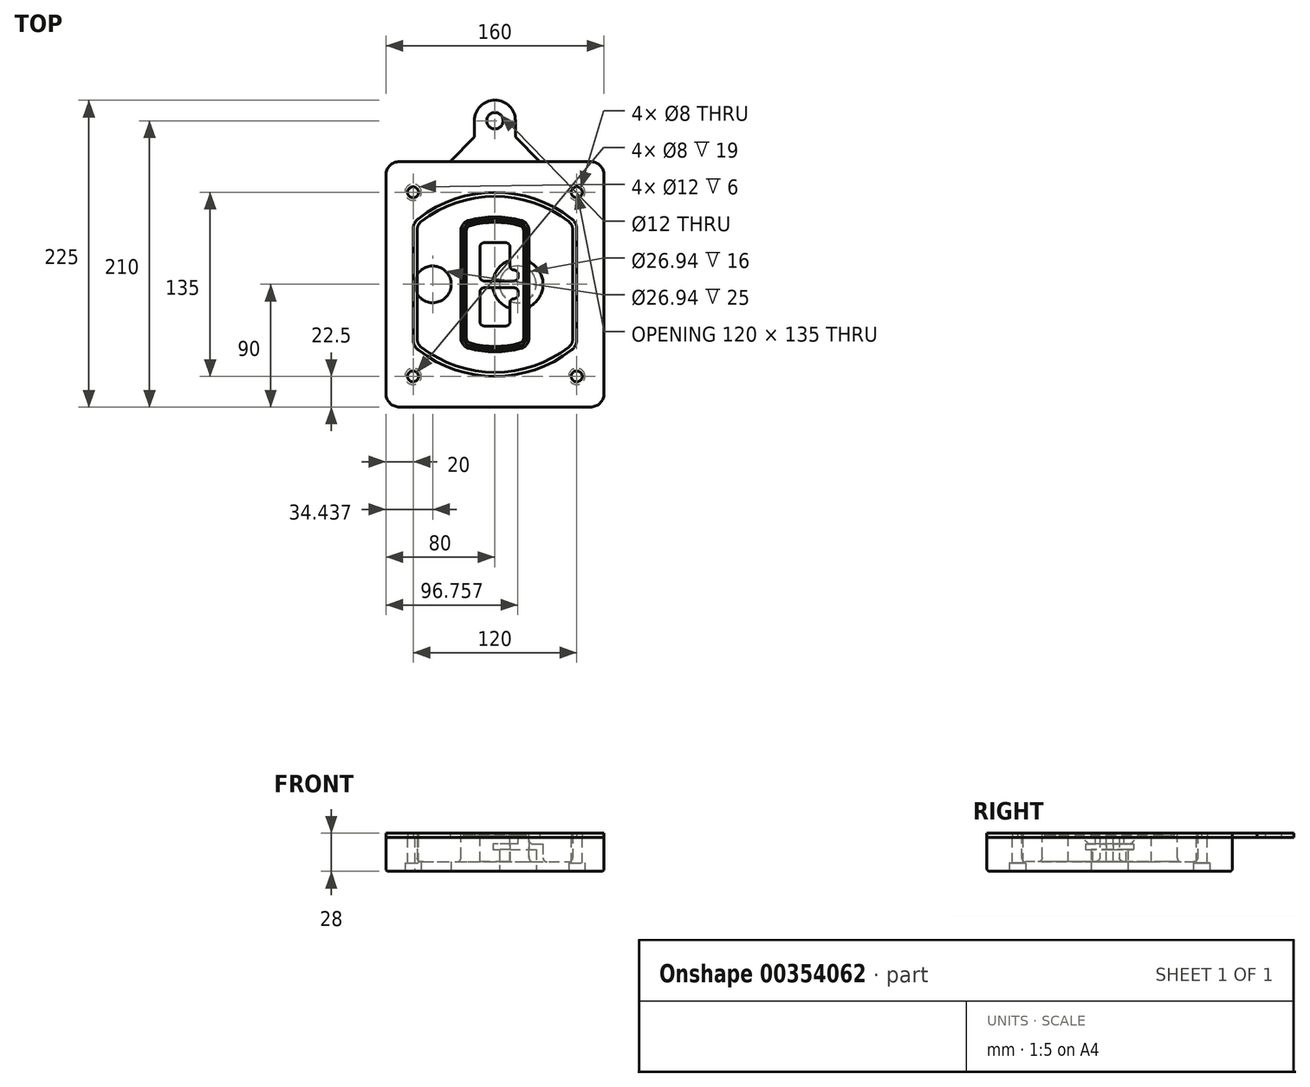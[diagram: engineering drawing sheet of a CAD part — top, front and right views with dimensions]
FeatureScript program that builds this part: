
annotation { "Feature Type Name" : "Feature", "Feature Type Description" : "" }
export const myFeature = defineFeature(function(context is Context, id is Id, definition is map)
    precondition{}
    {
        {
            var Q0;
            Q0=qCreatedBy(makeId("Top.planeOp"),FACE);
            var sketch = newSketch(context, id + "F0", { "sketchPlane" : qUnion([Q0])});
            skPoint(sketch, "E0.rect.middle", {"position": v(0, 0) * mm});
            skLineSegment(sketch, "E1.bottom", {"start": v(-70, -90) * mm, "end": v(70, -90) * mm});
            skLineSegment(sketch, "E1.top", {"start": v(-70, 90) * mm, "end": v(70, 90) * mm});
            skLineSegment(sketch, "E1.left", {"start": v(-80, -80) * mm, "end": v(-80, 80) * mm});
            skLineSegment(sketch, "E1.right", {"start": v(80, -80) * mm, "end": v(80, 80) * mm});
            skLineSegment(sketch, "E2", {"start": v(-80, 90) * mm, "end": v(80, -90) * mm, "construction": true});
            skLineSegment(sketch, "E3", {"start": v(80, 90) * mm, "end": v(-80, -90) * mm, "construction": true});
            skCircle(sketch, "E4", {"center": v(-60, 67.5) * mm, "radius": 4 * mm});
            skCircle(sketch, "E5", {"center": v(60, 67.5) * mm, "radius": 4 * mm});
            skCircle(sketch, "E6", {"center": v(60, -67.5) * mm, "radius": 4 * mm});
            skCircle(sketch, "E7", {"center": v(-60, -67.5) * mm, "radius": 4 * mm});
            skLineSegment(sketch, "E8", {"start": v(-60, 67.5) * mm, "end": v(60, 67.5) * mm, "construction": true});
            skLineSegment(sketch, "E9", {"start": v(60, 67.5) * mm, "end": v(60, -67.5) * mm, "construction": true});
            skLineSegment(sketch, "E10", {"start": v(60, -67.5) * mm, "end": v(-60, -67.5) * mm, "construction": true});
            skLineSegment(sketch, "E11", {"start": v(-60, -67.5) * mm, "end": v(-60, 67.5) * mm, "construction": true});
            skLineSegment(sketch, "E12", {"start": v(-60, 40.3) * mm, "end": v(-60, -40.3) * mm});
            skLineSegment(sketch, "E13", {"start": v(60, 40.3) * mm, "end": v(60, -40.3) * mm});
            skArc(sketch, "E14", {"start": v(56.15, 48.18) * mm, "mid": v(0, 67.5) * mm, "end": v(-56.15, 48.18) * mm});
            skArc(sketch, "E15", {"start": v(-56.15, -48.18) * mm, "mid": v(0, -67.5) * mm, "end": v(56.15, -48.18) * mm});
            skLineSegment(sketch, "E16", {"start": v(-60, 0) * mm, "end": v(60, 0) * mm, "construction": true});
            skPoint(sketch, "E17.visualSharp", {"position": v(-60, -45) * mm});
            skArc(sketch, "E17.filletArc", {"start": v(-60, -40.3) * mm, "mid": v(-58.99, -44.68) * mm, "end": v(-56.15, -48.18) * mm});
            skPoint(sketch, "E18.visualSharp", {"position": v(-60, 45) * mm});
            skArc(sketch, "E18.filletArc", {"start": v(-56.15, 48.18) * mm, "mid": v(-58.99, 44.68) * mm, "end": v(-60, 40.3) * mm});
            skPoint(sketch, "E19.visualSharp", {"position": v(60, 45) * mm});
            skArc(sketch, "E19.filletArc", {"start": v(60, 40.3) * mm, "mid": v(58.99, 44.68) * mm, "end": v(56.15, 48.18) * mm});
            skPoint(sketch, "E20.visualSharp", {"position": v(60, -45) * mm});
            skArc(sketch, "E20.filletArc", {"start": v(56.15, -48.18) * mm, "mid": v(58.99, -44.68) * mm, "end": v(60, -40.3) * mm});
            skPoint(sketch, "E21.visualSharp", {"position": v(-80, 90) * mm});
            skArc(sketch, "E21.filletArc", {"start": v(-70, 90) * mm, "mid": v(-77.07, 87.07) * mm, "end": v(-80, 80) * mm});
            skPoint(sketch, "E22.visualSharp", {"position": v(80, 90) * mm});
            skArc(sketch, "E22.filletArc", {"start": v(80, 80) * mm, "mid": v(77.07, 87.07) * mm, "end": v(70, 90) * mm});
            skPoint(sketch, "E23.visualSharp", {"position": v(80, -90) * mm});
            skArc(sketch, "E23.filletArc", {"start": v(70, -90) * mm, "mid": v(77.07, -87.07) * mm, "end": v(80, -80) * mm});
            skPoint(sketch, "E24.visualSharp", {"position": v(-80, -90) * mm});
            skArc(sketch, "E24.filletArc", {"start": v(-80, -80) * mm, "mid": v(-77.07, -87.07) * mm, "end": v(-70, -90) * mm});
            skArc(sketch, "E25.0", {"start": v(57, 40.3) * mm, "mid": v(56.3, 43.36) * mm, "end": v(54.3, 45.81) * mm});
            skLineSegment(sketch, "E25.1", {"start": v(57, 40.3) * mm, "end": v(57, -40.3) * mm});
            skArc(sketch, "E25.2", {"start": v(54.3, -45.81) * mm, "mid": v(56.3, -43.36) * mm, "end": v(57, -40.3) * mm});
            skArc(sketch, "E25.3", {"start": v(-54.3, -45.81) * mm, "mid": v(0, -64.5) * mm, "end": v(54.3, -45.81) * mm});
            skArc(sketch, "E25.4", {"start": v(-57, -40.3) * mm, "mid": v(-56.3, -43.36) * mm, "end": v(-54.3, -45.81) * mm});
            skArc(sketch, "E25.5", {"start": v(54.3, 45.81) * mm, "mid": v(0, 64.5) * mm, "end": v(-54.3, 45.81) * mm});
            skLineSegment(sketch, "E25.6", {"start": v(-57, 40.3) * mm, "end": v(-57, -40.3) * mm});
            skArc(sketch, "E25.7", {"start": v(-54.3, 45.81) * mm, "mid": v(-56.3, 43.36) * mm, "end": v(-57, 40.3) * mm});
            skArc(sketch, "E26.0", {"start": v(-58.62, 51.33) * mm, "mid": v(-62.58, 46.43) * mm, "end": v(-64, 40.3) * mm});
            skArc(sketch, "E26.1", {"start": v(58.62, 51.33) * mm, "mid": v(0, 71.5) * mm, "end": v(-58.62, 51.33) * mm});
            skArc(sketch, "E26.2", {"start": v(64, 40.3) * mm, "mid": v(62.58, 46.43) * mm, "end": v(58.62, 51.33) * mm});
            skLineSegment(sketch, "E26.3", {"start": v(64, 40.3) * mm, "end": v(64, -40.3) * mm});
            skArc(sketch, "E26.4", {"start": v(58.62, -51.33) * mm, "mid": v(62.58, -46.43) * mm, "end": v(64, -40.3) * mm});
            skLineSegment(sketch, "E26.5", {"start": v(-64, 40.3) * mm, "end": v(-64, -40.3) * mm});
            skArc(sketch, "E26.6", {"start": v(-58.62, -51.33) * mm, "mid": v(0, -71.5) * mm, "end": v(58.62, -51.33) * mm});
            skArc(sketch, "E26.7", {"start": v(-64, -40.3) * mm, "mid": v(-62.58, -46.43) * mm, "end": v(-58.62, -51.33) * mm});
            skSolve(sketch);
        }
        {
            var Q0;
            Q0=makeQuery(id+"F0.imprint","IMPRINT",FACE,{"disambiguationData":[TD([[makeQuery(id+"F0.imprint","IMPRINT",EDGE,{"derivedFrom":sQuery(id+"F0.wireOp",EDGE,"E1.bottom")}),1.0]])]});
            var Q1;
            Q1=makeQuery(id+"F0.imprint","IMPRINT",FACE,{"disambiguationData":[TD([[makeQuery(id+"F0.imprint","IMPRINT",EDGE,{"derivedFrom":sQuery(id+"F0.wireOp",EDGE,"E12")}),1.0]])]});
            var Q2;
            Q2=makeQuery(id+"F0.imprint","IMPRINT",FACE,{"disambiguationData":[TD([[makeQuery(id+"F0.imprint","IMPRINT",EDGE,{"derivedFrom":sQuery(id+"F0.wireOp",EDGE,"E25.0")}),1.0]])]});
            var Q3;
            Q3=makeQuery(id+"F0.imprint","IMPRINT",FACE,{"disambiguationData":[TD([[makeQuery(id+"F0.imprint","IMPRINT",EDGE,{"derivedFrom":sQuery(id+"F0.wireOp",EDGE,"E12")}),-1.0]])]});
            extrude(context, id + "F1", {"entities" : qUnion([Q0, Q1, Q2, Q3]), "oppositeDirection" : true, "depth" : 25 * mm});
        }
        {
            var Q0;
            Q0=makeQuery(id+"F0.imprint","IMPRINT",FACE,{"disambiguationData":[TD([[makeQuery(id+"F0.imprint","IMPRINT",EDGE,{"derivedFrom":sQuery(id+"F0.wireOp",EDGE,"E12")}),1.0]])]});
            extrude(context, id + "F2", {"entities" : qUnion([Q0]), "operationType" : NewBodyOperationType.ADD, "depth" : 3 * mm});
        }
        {
            var Q0;
            Q0=makeQuery(id+"F0.imprint","IMPRINT",FACE,{"disambiguationData":[TD([[makeQuery(id+"F0.imprint","IMPRINT",EDGE,{"derivedFrom":sQuery(id+"F0.wireOp",EDGE,"E25.0")}),1.0]])]});
            extrude(context, id + "F3", {"entities" : qUnion([Q0]), "operationType" : NewBodyOperationType.REMOVE, "oppositeDirection" : true, "depth" : 18 * mm});
        }
        {
            var Q0;
            Q0=makeQuery(id+"F2.opExtrude","CAP_FACE",FACE,{"disambiguationData":[OSD([sQuery(id+"F0.wireOp",EDGE,"E12"),sQuery(id+"F0.wireOp",EDGE,"E13"),sQuery(id+"F0.wireOp",EDGE,"E14"),sQuery(id+"F0.wireOp",EDGE,"E15"),sQuery(id+"F0.wireOp",EDGE,"E17.filletArc"),sQuery(id+"F0.wireOp",EDGE,"E18.filletArc"),sQuery(id+"F0.wireOp",EDGE,"E19.filletArc"),sQuery(id+"F0.wireOp",EDGE,"E20.filletArc"),sQuery(id+"F0.wireOp",EDGE,"E25.0"),sQuery(id+"F0.wireOp",EDGE,"E25.1"),sQuery(id+"F0.wireOp",EDGE,"E25.2"),sQuery(id+"F0.wireOp",EDGE,"E25.3"),sQuery(id+"F0.wireOp",EDGE,"E25.4"),sQuery(id+"F0.wireOp",EDGE,"E25.5"),sQuery(id+"F0.wireOp",EDGE,"E25.6"),sQuery(id+"F0.wireOp",EDGE,"E25.7")])],"isStart":false});
            var sketch = newSketch(context, id + "F4", { "sketchPlane" : qUnion([Q0])});
            skArc(sketch, "E27.0", {"start": v(-19.08, -46.97) * mm, "mid": v(0, -49.5) * mm, "end": v(19.08, -46.97) * mm});
            skArc(sketch, "E28.0", {"start": v(19.08, 46.97) * mm, "mid": v(0, 49.5) * mm, "end": v(-19.08, 46.97) * mm});
            skLineSegment(sketch, "E29", {"start": v(-25, 39.25) * mm, "end": v(-25, -39.25) * mm});
            skLineSegment(sketch, "E30", {"start": v(25, 39.25) * mm, "end": v(25, -39.25) * mm});
            skLineSegment(sketch, "E31", {"start": v(-25, 45.1) * mm, "end": v(25, 45.1) * mm, "construction": true});
            skLineSegment(sketch, "E32", {"start": v(-25, -45.1) * mm, "end": v(25, -45.1) * mm, "construction": true});
            skPoint(sketch, "E33.visualSharp", {"position": v(-25, 45.1) * mm});
            skArc(sketch, "E33.filletArc", {"start": v(-19.08, 46.97) * mm, "mid": v(-23.35, 44.11) * mm, "end": v(-25, 39.25) * mm});
            skPoint(sketch, "E34.visualSharp", {"position": v(25, 45.1) * mm});
            skArc(sketch, "E34.filletArc", {"start": v(25, 39.25) * mm, "mid": v(23.35, 44.11) * mm, "end": v(19.08, 46.97) * mm});
            skPoint(sketch, "E35.visualSharp", {"position": v(25, -45.1) * mm});
            skArc(sketch, "E35.filletArc", {"start": v(19.08, -46.97) * mm, "mid": v(23.35, -44.11) * mm, "end": v(25, -39.25) * mm});
            skPoint(sketch, "E36.visualSharp", {"position": v(-25, -45.1) * mm});
            skArc(sketch, "E36.filletArc", {"start": v(-25, -39.25) * mm, "mid": v(-23.35, -44.11) * mm, "end": v(-19.08, -46.97) * mm});
            skArc(sketch, "E37.0", {"start": v(54.3, 45.81) * mm, "mid": v(0, 64.5) * mm, "end": v(-54.3, 45.81) * mm});
            skArc(sketch, "E37.1", {"start": v(-54.3, 45.81) * mm, "mid": v(-56.3, 43.36) * mm, "end": v(-57, 40.3) * mm});
            skLineSegment(sketch, "E37.2", {"start": v(-57, 40.3) * mm, "end": v(-57, -40.3) * mm});
            skArc(sketch, "E37.3", {"start": v(-57, -40.3) * mm, "mid": v(-56.3, -43.36) * mm, "end": v(-54.3, -45.81) * mm});
            skArc(sketch, "E37.4", {"start": v(-54.3, -45.81) * mm, "mid": v(0, -64.5) * mm, "end": v(54.3, -45.81) * mm});
            skArc(sketch, "E37.5", {"start": v(54.3, -45.81) * mm, "mid": v(56.3, -43.36) * mm, "end": v(57, -40.3) * mm});
            skLineSegment(sketch, "E37.6", {"start": v(57, 40.3) * mm, "end": v(57, -40.3) * mm});
            skArc(sketch, "E37.7", {"start": v(57, 40.3) * mm, "mid": v(56.3, 43.36) * mm, "end": v(54.3, 45.81) * mm});
            skLineSegment(sketch, "E38.0", {"start": v(23, 39.25) * mm, "end": v(23, -39.25) * mm});
            skArc(sketch, "E38.1", {"start": v(18.56, -45.04) * mm, "mid": v(21.76, -42.9) * mm, "end": v(23, -39.25) * mm});
            skArc(sketch, "E38.2", {"start": v(-18.56, -45.04) * mm, "mid": v(0, -47.5) * mm, "end": v(18.56, -45.04) * mm});
            skArc(sketch, "E38.3", {"start": v(-23, -39.25) * mm, "mid": v(-21.76, -42.9) * mm, "end": v(-18.56, -45.04) * mm});
            skLineSegment(sketch, "E38.4", {"start": v(-23, 39.25) * mm, "end": v(-23, -39.25) * mm});
            skArc(sketch, "E38.5", {"start": v(23, 39.25) * mm, "mid": v(21.76, 42.9) * mm, "end": v(18.56, 45.04) * mm});
            skArc(sketch, "E38.6", {"start": v(-18.56, 45.04) * mm, "mid": v(-21.76, 42.9) * mm, "end": v(-23, 39.25) * mm});
            skArc(sketch, "E38.7", {"start": v(18.56, 45.04) * mm, "mid": v(0, 47.5) * mm, "end": v(-18.56, 45.04) * mm});
            skArc(sketch, "E39.0", {"start": v(21, 39.25) * mm, "mid": v(20.18, 41.68) * mm, "end": v(18.04, 43.1) * mm});
            skLineSegment(sketch, "E39.1", {"start": v(21, 39.25) * mm, "end": v(21, -39.25) * mm});
            skArc(sketch, "E39.2", {"start": v(18.04, -43.1) * mm, "mid": v(20.18, -41.68) * mm, "end": v(21, -39.25) * mm});
            skArc(sketch, "E39.3", {"start": v(-18.04, -43.1) * mm, "mid": v(0, -45.5) * mm, "end": v(18.04, -43.1) * mm});
            skArc(sketch, "E39.4", {"start": v(-21, -39.25) * mm, "mid": v(-20.18, -41.68) * mm, "end": v(-18.04, -43.1) * mm});
            skArc(sketch, "E39.5", {"start": v(18.04, 43.1) * mm, "mid": v(0, 45.5) * mm, "end": v(-18.04, 43.1) * mm});
            skLineSegment(sketch, "E39.6", {"start": v(-21, 39.25) * mm, "end": v(-21, -39.25) * mm});
            skArc(sketch, "E39.7", {"start": v(-18.04, 43.1) * mm, "mid": v(-20.18, 41.68) * mm, "end": v(-21, 39.25) * mm});
            skLineSegment(sketch, "E40", {"start": v(-25, 0) * mm, "end": v(25, 0) * mm, "construction": true});
            skLineSegment(sketch, "E41", {"start": v(-11, 5.5) * mm, "end": v(-11, 27.5) * mm});
            skLineSegment(sketch, "E42", {"start": v(-8, 30.5) * mm, "end": v(8, 30.5) * mm});
            skLineSegment(sketch, "E43", {"start": v(11, 27.5) * mm, "end": v(11, 13.5) * mm});
            skLineSegment(sketch, "E44", {"start": v(14, 10.5) * mm, "end": v(14, 10.5) * mm});
            skLineSegment(sketch, "E45", {"start": v(17, 7.5) * mm, "end": v(17, 5.5) * mm});
            skLineSegment(sketch, "E46", {"start": v(14, 2.5) * mm, "end": v(-8, 2.5) * mm});
            skPoint(sketch, "E47.visualSharp", {"position": v(-11, 30.5) * mm});
            skArc(sketch, "E47.filletArc", {"start": v(-8, 30.5) * mm, "mid": v(-10.12, 29.62) * mm, "end": v(-11, 27.5) * mm});
            skPoint(sketch, "E48.visualSharp", {"position": v(11, 30.5) * mm});
            skArc(sketch, "E48.filletArc", {"start": v(11, 27.5) * mm, "mid": v(10.12, 29.62) * mm, "end": v(8, 30.5) * mm});
            skPoint(sketch, "E49.visualSharp", {"position": v(11, 10.5) * mm});
            skArc(sketch, "E49.filletArc", {"start": v(11, 13.5) * mm, "mid": v(11.88, 11.38) * mm, "end": v(14, 10.5) * mm});
            skPoint(sketch, "E50.visualSharp", {"position": v(17, 10.5) * mm});
            skArc(sketch, "E50.filletArc", {"start": v(17, 7.5) * mm, "mid": v(16.12, 9.62) * mm, "end": v(14, 10.5) * mm});
            skPoint(sketch, "E51.visualSharp", {"position": v(17, 2.5) * mm});
            skArc(sketch, "E51.filletArc", {"start": v(14, 2.5) * mm, "mid": v(16.12, 3.38) * mm, "end": v(17, 5.5) * mm});
            skPoint(sketch, "E52.visualSharp", {"position": v(-11, 2.5) * mm});
            skArc(sketch, "E52.filletArc", {"start": v(-11, 5.5) * mm, "mid": v(-10.12, 3.38) * mm, "end": v(-8, 2.5) * mm});
            skLineSegment(sketch, "E53.0.MirrorCS", {"start": v(14, -2.5) * mm, "end": v(-8, -2.5) * mm});
            skArc(sketch, "E54.0.MirrorCS", {"start": v(-11, -5.5) * mm, "mid": v(-10.12, -3.38) * mm, "end": v(-8, -2.5) * mm});
            skLineSegment(sketch, "E55.0.MirrorCS", {"start": v(-11, -5.5) * mm, "end": v(-11, -27.5) * mm});
            skArc(sketch, "E56.0.MirrorCS", {"start": v(-8, -30.5) * mm, "mid": v(-10.12, -29.62) * mm, "end": v(-11, -27.5) * mm});
            skLineSegment(sketch, "E57.0.MirrorCS", {"start": v(-8, -30.5) * mm, "end": v(8, -30.5) * mm});
            skArc(sketch, "E58.0.MirrorCS", {"start": v(11, -27.5) * mm, "mid": v(10.12, -29.62) * mm, "end": v(8, -30.5) * mm});
            skLineSegment(sketch, "E59.0.MirrorCS", {"start": v(11, -27.5) * mm, "end": v(11, -13.5) * mm});
            skArc(sketch, "E60.0.MirrorCS", {"start": v(11, -13.5) * mm, "mid": v(11.88, -11.38) * mm, "end": v(14, -10.5) * mm});
            skArc(sketch, "E61.0.MirrorCS", {"start": v(17, -7.5) * mm, "mid": v(16.12, -9.62) * mm, "end": v(14, -10.5) * mm});
            skLineSegment(sketch, "E62.0.MirrorCS", {"start": v(17, -7.5) * mm, "end": v(17, -5.5) * mm});
            skArc(sketch, "E63.0.MirrorCS", {"start": v(14, -2.5) * mm, "mid": v(16.12, -3.38) * mm, "end": v(17, -5.5) * mm});
            skSolve(sketch);
        }
        {
            var Q0;
            Q0=makeQuery(id+"F4.imprint","IMPRINT",FACE,{"disambiguationData":[TD([[makeQuery(id+"F4.imprint","IMPRINT",EDGE,{"derivedFrom":sQuery(id+"F4.wireOp",EDGE,"E27.0")}),1.0]])]});
            var Q1;
            Q1=makeQuery(id+"F4.imprint","IMPRINT",FACE,{"disambiguationData":[TD([[makeQuery(id+"F4.imprint","IMPRINT",EDGE,{"derivedFrom":sQuery(id+"F4.wireOp",EDGE,"E38.0")}),-1.0]])]});
            var Q2;
            Q2=makeQuery(id+"F4.imprint","IMPRINT",FACE,{"disambiguationData":[TD([[makeQuery(id+"F4.imprint","IMPRINT",EDGE,{"derivedFrom":sQuery(id+"F4.wireOp",EDGE,"E39.0")}),1.0]])]});
            extrude(context, id + "F5", {"entities" : qUnion([Q0, Q1, Q2]), "operationType" : NewBodyOperationType.ADD, "endBound" : BoundingType.UP_TO_NEXT, "oppositeDirection" : true, "depth" : 25 * mm});
        }
        {
            var Q0;
            Q0=makeQuery(id+"F4.imprint","IMPRINT",FACE,{"disambiguationData":[TD([[makeQuery(id+"F4.imprint","IMPRINT",EDGE,{"derivedFrom":sQuery(id+"F4.wireOp",EDGE,"E38.0")}),-1.0]])]});
            extrude(context, id + "F6", {"entities" : qUnion([Q0]), "operationType" : NewBodyOperationType.REMOVE, "oppositeDirection" : true, "depth" : 2 * mm});
        }
        {
            var Q0;
            Q0=makeQuery(id+"F1.opExtrude","CAP_FACE",FACE,{"disambiguationData":[OSD([sQuery(id+"F0.wireOp",EDGE,"E1.bottom"),sQuery(id+"F0.wireOp",EDGE,"E1.top"),sQuery(id+"F0.wireOp",EDGE,"E1.left"),sQuery(id+"F0.wireOp",EDGE,"E1.right"),sQuery(id+"F0.wireOp",EDGE,"E4"),sQuery(id+"F0.wireOp",EDGE,"E5"),sQuery(id+"F0.wireOp",EDGE,"E6"),sQuery(id+"F0.wireOp",EDGE,"E7"),sQuery(id+"F0.wireOp",EDGE,"E21.filletArc"),sQuery(id+"F0.wireOp",EDGE,"E22.filletArc"),sQuery(id+"F0.wireOp",EDGE,"E23.filletArc"),sQuery(id+"F0.wireOp",EDGE,"E24.filletArc")])],"isStart":false});
            var sketch = newSketch(context, id + "F7", { "sketchPlane" : qUnion([Q0])});
            skCircle(sketch, "E64", {"center": v(16.76, 0) * mm, "radius": 13.47 * mm});
            skCircle(sketch, "E65", {"center": v(-45.56, 0) * mm, "radius": 13.47 * mm});
            skLineSegment(sketch, "E66", {"start": v(80, 0) * mm, "end": v(-80, 0) * mm});
            skCircle(sketch, "E67", {"center": v(16.76, 0) * mm, "radius": 18.47 * mm});
            skCircle(sketch, "E68", {"center": v(60, -67.5) * mm, "radius": 6 * mm});
            skCircle(sketch, "E69", {"center": v(-60, -67.5) * mm, "radius": 6 * mm});
            skCircle(sketch, "E70", {"center": v(-60, 67.5) * mm, "radius": 6 * mm});
            skCircle(sketch, "E71", {"center": v(60, 67.5) * mm, "radius": 6 * mm});
            skSolve(sketch);
        }
        {
            var Q0;
            {var subQ1=sQuery(id+"F7.wireOp",EDGE,"E66");var subQ4=sQuery(id+"F7.wireOp",EDGE,"E64");var subQ6=makeQuery(id+"F7.imprint","INTERSECT",VERTEX,{"disambiguationData":[OD(0.0)],"derivedFrom":[subQ4,subQ1]});Q0=makeQuery(id+"F7.imprint","IMPRINT",FACE,{"disambiguationData":[TD([[makeQuery(id+"F7.imprint","IMPRINT",EDGE,{"disambiguationData":[TD([[subQ6,-1.0]])],"derivedFrom":subQ4}),-1.0]])]});}
            var Q1;
            {var subQ0=sQuery(id+"F7.wireOp",EDGE,"E66");var subQ1=sQuery(id+"F7.wireOp",EDGE,"E64");var subQ3=makeQuery(id+"F7.imprint","INTERSECT",VERTEX,{"disambiguationData":[OD(0.0)],"derivedFrom":[subQ1,subQ0]});Q1=makeQuery(id+"F7.imprint","IMPRINT",FACE,{"disambiguationData":[TD([[makeQuery(id+"F7.imprint","IMPRINT",EDGE,{"disambiguationData":[TD([[subQ3,-1.0]])],"derivedFrom":subQ1}),1.0]])]});}
            var Q2;
            {var subQ0=sQuery(id+"F7.wireOp",EDGE,"E66");var subQ1=sQuery(id+"F7.wireOp",EDGE,"E64");var subQ3=makeQuery(id+"F7.imprint","INTERSECT",VERTEX,{"disambiguationData":[OD(0.0)],"derivedFrom":[subQ1,subQ0]});Q2=makeQuery(id+"F7.imprint","IMPRINT",FACE,{"disambiguationData":[TD([[makeQuery(id+"F7.imprint","IMPRINT",EDGE,{"disambiguationData":[TD([[subQ3,1.0]])],"derivedFrom":subQ1}),1.0]])]});}
            var Q3;
            {var subQ1=sQuery(id+"F7.wireOp",EDGE,"E66");var subQ4=sQuery(id+"F7.wireOp",EDGE,"E64");var subQ6=makeQuery(id+"F7.imprint","INTERSECT",VERTEX,{"disambiguationData":[OD(0.0)],"derivedFrom":[subQ4,subQ1]});Q3=makeQuery(id+"F7.imprint","IMPRINT",FACE,{"disambiguationData":[TD([[makeQuery(id+"F7.imprint","IMPRINT",EDGE,{"disambiguationData":[TD([[subQ6,1.0]])],"derivedFrom":subQ4}),-1.0]])]});}
            extrude(context, id + "F8", {"entities" : qUnion([Q0, Q1, Q2, Q3]), "operationType" : NewBodyOperationType.ADD, "oppositeDirection" : true, "depth" : 20 * mm});
        }
        {
            var Q0;
            {var subQ0=sQuery(id+"F7.wireOp",EDGE,"E66");var subQ1=sQuery(id+"F7.wireOp",EDGE,"E64");var subQ3=makeQuery(id+"F7.imprint","INTERSECT",VERTEX,{"disambiguationData":[OD(0.0)],"derivedFrom":[subQ1,subQ0]});Q0=makeQuery(id+"F7.imprint","IMPRINT",FACE,{"disambiguationData":[TD([[makeQuery(id+"F7.imprint","IMPRINT",EDGE,{"disambiguationData":[TD([[subQ3,-1.0]])],"derivedFrom":subQ1}),1.0]])]});}
            var Q1;
            {var subQ0=sQuery(id+"F7.wireOp",EDGE,"E66");var subQ1=sQuery(id+"F7.wireOp",EDGE,"E64");var subQ3=makeQuery(id+"F7.imprint","INTERSECT",VERTEX,{"disambiguationData":[OD(0.0)],"derivedFrom":[subQ1,subQ0]});Q1=makeQuery(id+"F7.imprint","IMPRINT",FACE,{"disambiguationData":[TD([[makeQuery(id+"F7.imprint","IMPRINT",EDGE,{"disambiguationData":[TD([[subQ3,1.0]])],"derivedFrom":subQ1}),1.0]])]});}
            extrude(context, id + "F9", {"entities" : qUnion([Q0, Q1]), "operationType" : NewBodyOperationType.REMOVE, "oppositeDirection" : true, "depth" : 16 * mm});
        }
        {
            var Q0;
            {var subQ0=sQuery(id+"F7.wireOp",EDGE,"E66");var subQ1=sQuery(id+"F7.wireOp",EDGE,"E65");var subQ3=makeQuery(id+"F7.imprint","INTERSECT",VERTEX,{"disambiguationData":[OD(0.0)],"derivedFrom":[subQ1,subQ0]});Q0=makeQuery(id+"F7.imprint","IMPRINT",FACE,{"disambiguationData":[TD([[makeQuery(id+"F7.imprint","IMPRINT",EDGE,{"disambiguationData":[TD([[subQ3,-1.0]])],"derivedFrom":subQ1}),1.0]])]});}
            var Q1;
            {var subQ0=sQuery(id+"F7.wireOp",EDGE,"E66");var subQ1=sQuery(id+"F7.wireOp",EDGE,"E65");var subQ3=makeQuery(id+"F7.imprint","INTERSECT",VERTEX,{"disambiguationData":[OD(0.0)],"derivedFrom":[subQ1,subQ0]});Q1=makeQuery(id+"F7.imprint","IMPRINT",FACE,{"disambiguationData":[TD([[makeQuery(id+"F7.imprint","IMPRINT",EDGE,{"disambiguationData":[TD([[subQ3,1.0]])],"derivedFrom":subQ1}),1.0]])]});}
            extrude(context, id + "F10", {"entities" : qUnion([Q0, Q1]), "operationType" : NewBodyOperationType.REMOVE, "oppositeDirection" : true, "depth" : 25 * mm});
        }
        {
            var Q0;
            Q0=makeQuery(id+"F7.imprint","IMPRINT",FACE,{"disambiguationData":[TD([[makeQuery(id+"F7.imprint","IMPRINT",EDGE,{"derivedFrom":sQuery(id+"F7.wireOp",EDGE,"E68")}),1.0]])]});
            var Q1;
            Q1=makeQuery(id+"F7.imprint","IMPRINT",FACE,{"disambiguationData":[TD([[makeQuery(id+"F7.imprint","IMPRINT",EDGE,{"derivedFrom":makeQuery(id+"F1.opExtrude","CAP_EDGE",EDGE,{"disambiguationData":[OSD([sQuery(id+"F0.wireOp",EDGE,"E5")])],"isStart":false})}),-1.0]])]});
            var Q2;
            Q2=makeQuery(id+"F7.imprint","IMPRINT",FACE,{"disambiguationData":[TD([[makeQuery(id+"F7.imprint","IMPRINT",EDGE,{"derivedFrom":sQuery(id+"F7.wireOp",EDGE,"E69")}),1.0]])]});
            var Q3;
            Q3=makeQuery(id+"F7.imprint","IMPRINT",FACE,{"disambiguationData":[TD([[makeQuery(id+"F7.imprint","IMPRINT",EDGE,{"derivedFrom":makeQuery(id+"F1.opExtrude","CAP_EDGE",EDGE,{"disambiguationData":[OSD([sQuery(id+"F0.wireOp",EDGE,"E4")])],"isStart":false})}),-1.0]])]});
            var Q4;
            Q4=makeQuery(id+"F7.imprint","IMPRINT",FACE,{"disambiguationData":[TD([[makeQuery(id+"F7.imprint","IMPRINT",EDGE,{"derivedFrom":sQuery(id+"F7.wireOp",EDGE,"E70")}),1.0]])]});
            var Q5;
            Q5=makeQuery(id+"F7.imprint","IMPRINT",FACE,{"disambiguationData":[TD([[makeQuery(id+"F7.imprint","IMPRINT",EDGE,{"derivedFrom":makeQuery(id+"F1.opExtrude","CAP_EDGE",EDGE,{"disambiguationData":[OSD([sQuery(id+"F0.wireOp",EDGE,"E7")])],"isStart":false})}),-1.0]])]});
            var Q6;
            Q6=makeQuery(id+"F7.imprint","IMPRINT",FACE,{"disambiguationData":[TD([[makeQuery(id+"F7.imprint","IMPRINT",EDGE,{"derivedFrom":sQuery(id+"F7.wireOp",EDGE,"E71")}),1.0]])]});
            var Q7;
            Q7=makeQuery(id+"F7.imprint","IMPRINT",FACE,{"disambiguationData":[TD([[makeQuery(id+"F7.imprint","IMPRINT",EDGE,{"derivedFrom":makeQuery(id+"F1.opExtrude","CAP_EDGE",EDGE,{"disambiguationData":[OSD([sQuery(id+"F0.wireOp",EDGE,"E6")])],"isStart":false})}),-1.0]])]});
            extrude(context, id + "F11", {"entities" : qUnion([Q0, Q1, Q2, Q3, Q4, Q5, Q6, Q7]), "operationType" : NewBodyOperationType.REMOVE, "oppositeDirection" : true, "depth" : 6 * mm});
        }
        {
            var Q0;
            Q0=makeQuery(id+"F9.boolean.opBoolean","COPY",FACE,{"derivedFrom":makeQuery(id+"F9.opExtrude","CAP_FACE",FACE,{"disambiguationData":[OSD([sQuery(id+"F7.wireOp",EDGE,"E64")])],"isStart":false})});
            var sketch = newSketch(context, id + "F12", { "sketchPlane" : qUnion([Q0])});
            skArc(sketch, "E72.0", {"start": v(11, 17.55) * mm, "mid": v(2.57, 11.82) * mm, "end": v(-1.54, 2.5) * mm});
            skArc(sketch, "E72.1", {"start": v(-1.54, -2.5) * mm, "mid": v(2.57, -11.82) * mm, "end": v(11, -17.55) * mm});
            skLineSegment(sketch, "E73", {"start": v(-1.54, -2.5) * mm, "end": v(14, -2.5) * mm});
            skLineSegment(sketch, "E74.0", {"start": v(14, 2.5) * mm, "end": v(-1.54, 2.5) * mm});
            skArc(sketch, "E74.1", {"start": v(14, 2.5) * mm, "mid": v(16.12, 3.38) * mm, "end": v(17, 5.5) * mm});
            skLineSegment(sketch, "E74.2", {"start": v(17, 7.5) * mm, "end": v(17, 5.5) * mm});
            skArc(sketch, "E74.3", {"start": v(17, 7.5) * mm, "mid": v(16.12, 9.62) * mm, "end": v(14, 10.5) * mm});
            skArc(sketch, "E74.4", {"start": v(11, 13.5) * mm, "mid": v(11.88, 11.38) * mm, "end": v(14, 10.5) * mm});
            skLineSegment(sketch, "E74.5", {"start": v(11, 17.55) * mm, "end": v(11, 13.5) * mm});
            skLineSegment(sketch, "E74.7", {"start": v(14, -2.5) * mm, "end": v(-1.54, -2.5) * mm});
            skArc(sketch, "E74.8", {"start": v(14, -2.5) * mm, "mid": v(16.12, -3.38) * mm, "end": v(17, -5.5) * mm});
            skLineSegment(sketch, "E74.9", {"start": v(17, -7.5) * mm, "end": v(17, -5.5) * mm});
            skArc(sketch, "E74.10", {"start": v(17, -7.5) * mm, "mid": v(16.12, -9.62) * mm, "end": v(14, -10.5) * mm});
            skArc(sketch, "E74.11", {"start": v(11, -13.5) * mm, "mid": v(11.88, -11.38) * mm, "end": v(14, -10.5) * mm});
            skLineSegment(sketch, "E74.12", {"start": v(11, -17.55) * mm, "end": v(11, -13.5) * mm});
            skPoint(sketch, "E75.orphan", {"position": v(11, -27.5) * mm});
            skPoint(sketch, "E76.orphan", {"position": v(-8, -2.5) * mm});
            skPoint(sketch, "E77.orphan", {"position": v(-8, 2.5) * mm});
            skPoint(sketch, "E78.orphan", {"position": v(11, 27.5) * mm});
            skSolve(sketch);
        }
        {
            var Q0;
            {var subQ7=sQuery(id+"F12.wireOp",EDGE,"E72.0");var subQ14=sQuery(id+"F12.wireOp",EDGE,"E72.1");var subQ16=sQuery(id+"F12.wireOp",EDGE,"E74.1");var subQ18=sQuery(id+"F12.wireOp",EDGE,"E74.8");Q0=qUnion([makeQuery(id+"F12.imprint","IMPRINT",FACE,{"disambiguationData":[TD([[makeQuery(id+"F12.imprint","IMPRINT",EDGE,{"derivedFrom":subQ7}),1.0]])]}),makeQuery(id+"F12.imprint","IMPRINT",FACE,{"disambiguationData":[TD([[makeQuery(id+"F12.imprint","IMPRINT",EDGE,{"derivedFrom":subQ14}),1.0]])]}),makeQuery(id+"F12.imprint","IMPRINT",FACE,{"disambiguationData":[TD([[makeQuery(id+"F12.imprint","IMPRINT",EDGE,{"derivedFrom":subQ16}),1.0]])]}),makeQuery(id+"F12.imprint","IMPRINT",FACE,{"disambiguationData":[TD([[makeQuery(id+"F12.imprint","IMPRINT",EDGE,{"derivedFrom":subQ18}),-1.0]])]})]);}
            var Q1;
            Q1=makeQuery(id+"F5.boolean.opBoolean","SPLIT",FACE,{"disambiguationData":[TD([makeQuery(id+"F5.opExtrude","SWEPT_FACE",FACE,{"disambiguationData":[OSD([sQuery(id+"F4.wireOp",EDGE,"E41")])]})])],"derivedFrom":makeQuery(id+"F3.boolean.opBoolean","COPY",FACE,{"derivedFrom":makeQuery(id+"F3.opExtrude","CAP_FACE",FACE,{"disambiguationData":[OSD([sQuery(id+"F0.wireOp",EDGE,"E25.0"),sQuery(id+"F0.wireOp",EDGE,"E25.1"),sQuery(id+"F0.wireOp",EDGE,"E25.2"),sQuery(id+"F0.wireOp",EDGE,"E25.3"),sQuery(id+"F0.wireOp",EDGE,"E25.4"),sQuery(id+"F0.wireOp",EDGE,"E25.5"),sQuery(id+"F0.wireOp",EDGE,"E25.6"),sQuery(id+"F0.wireOp",EDGE,"E25.7")])],"isStart":false})})});
            extrude(context, id + "F13", {"entities" : qUnion([Q0]), "operationType" : NewBodyOperationType.REMOVE, "endBound" : BoundingType.UP_TO_SURFACE, "endBoundEntityFace" : qUnion([Q1]), "depth" : 25 * mm});
        }
        {
            var Q0;
            Q0=makeQuery(id+"F3.boolean.opBoolean","COPY",EDGE,{"derivedFrom":makeQuery(id+"F3.opExtrude","CAP_EDGE",EDGE,{"disambiguationData":[OSD([sQuery(id+"F0.wireOp",EDGE,"E25.6")])],"isStart":false})});
            var Q1;
            Q1=makeQuery(id+"F8.boolean.opBoolean","INTERSECT",EDGE,{"derivedFrom":[makeQuery(id+"F5.opExtrude","SWEPT_FACE",FACE,{"disambiguationData":[OSD([sQuery(id+"F4.wireOp",EDGE,"E30")])]}),makeQuery(id+"F8.opExtrude","CAP_FACE",FACE,{"disambiguationData":[OSD([sQuery(id+"F7.wireOp",EDGE,"E67")])],"isStart":false})]});
            var Q2;
            Q2=makeQuery(id+"F8.boolean.opBoolean","INTERSECT",EDGE,{"disambiguationData":[OD(1.0)],"derivedFrom":[makeQuery(id+"F5.opExtrude","SWEPT_FACE",FACE,{"disambiguationData":[OSD([sQuery(id+"F4.wireOp",EDGE,"E30")])]}),makeQuery(id+"F8.opExtrude","SWEPT_FACE",FACE,{"disambiguationData":[OSD([sQuery(id+"F7.wireOp",EDGE,"E67")])]})]});
            var Q3;
            {var subQ0=sQuery(id+"F4.wireOp",EDGE,"E30");Q3=makeQuery(id+"F8.boolean.opBoolean","SPLIT",EDGE,{"disambiguationData":[TD([makeQuery(id+"F5.opExtrude","SWEPT_FACE",FACE,{"disambiguationData":[OSD([sQuery(id+"F4.wireOp",EDGE,"E35.filletArc")])]})])],"derivedFrom":makeQuery(id+"F5.opExtrude","CAP_EDGE",EDGE,{"disambiguationData":[OSD([subQ0])],"isStart":false})});}
            var Q4;
            {var subQ0=sQuery(id+"F0.wireOp",EDGE,"E25.7");var subQ1=sQuery(id+"F0.wireOp",EDGE,"E25.1");var subQ2=sQuery(id+"F0.wireOp",EDGE,"E25.6");var subQ3=sQuery(id+"F0.wireOp",EDGE,"E25.5");var subQ4=sQuery(id+"F0.wireOp",EDGE,"E25.4");var subQ5=sQuery(id+"F0.wireOp",EDGE,"E25.0");var subQ6=sQuery(id+"F0.wireOp",EDGE,"E25.2");var subQ7=sQuery(id+"F0.wireOp",EDGE,"E25.3");Q4=makeQuery(id+"F8.boolean.opBoolean","INTERSECT",EDGE,{"derivedFrom":[makeQuery(id+"F5.boolean.opBoolean","SPLIT",FACE,{"disambiguationData":[TD([makeQuery(id+"F2.opExtrude","SWEPT_FACE",FACE,{"disambiguationData":[OSD([subQ5])]})])],"derivedFrom":makeQuery(id+"F3.boolean.opBoolean","COPY",FACE,{"derivedFrom":makeQuery(id+"F3.opExtrude","CAP_FACE",FACE,{"disambiguationData":[OSD([subQ5,subQ1,subQ6,subQ7,subQ4,subQ3,subQ2,subQ0])],"isStart":false})})}),makeQuery(id+"F8.opExtrude","SWEPT_FACE",FACE,{"disambiguationData":[OSD([sQuery(id+"F7.wireOp",EDGE,"E67")])]})]});}
            var Q5;
            Q5=makeQuery(id+"F8.boolean.opBoolean","INTERSECT",EDGE,{"disambiguationData":[OD(0.0)],"derivedFrom":[makeQuery(id+"F5.opExtrude","SWEPT_FACE",FACE,{"disambiguationData":[OSD([sQuery(id+"F4.wireOp",EDGE,"E30")])]}),makeQuery(id+"F8.opExtrude","SWEPT_FACE",FACE,{"disambiguationData":[OSD([sQuery(id+"F7.wireOp",EDGE,"E67")])]})]});
            fillet(context, id + "F14", {"entities" : qUnion([Q0, Q1, Q2, Q3, Q4, Q5]), "radius" : 3 * mm, "tangentPropagation" : true, "allowEdgeOverflow" : false});
        }
        {
            var Q0;
            Q0=makeQuery(id+"F1.opExtrude","CAP_EDGE",EDGE,{"disambiguationData":[OSD([sQuery(id+"F0.wireOp",EDGE,"E1.bottom")])],"isStart":false});
            fillet(context, id + "F15", {"entities" : qUnion([Q0]), "radius" : 2 * mm, "tangentPropagation" : true, "allowEdgeOverflow" : false});
        }
        {
            var Q0;
            {var subQ0=sQuery(id+"F0.wireOp",EDGE,"E21.filletArc");var subQ1=sQuery(id+"F0.wireOp",EDGE,"E7");var subQ2=sQuery(id+"F0.wireOp",EDGE,"E6");var subQ3=sQuery(id+"F0.wireOp",EDGE,"E5");var subQ4=sQuery(id+"F0.wireOp",EDGE,"E4");var subQ5=sQuery(id+"F0.wireOp",EDGE,"E22.filletArc");var subQ6=sQuery(id+"F0.wireOp",EDGE,"E1.bottom");var subQ7=sQuery(id+"F0.wireOp",EDGE,"E1.right");var subQ8=sQuery(id+"F0.wireOp",EDGE,"E1.top");var subQ9=sQuery(id+"F0.wireOp",EDGE,"E1.left");var subQ10=sQuery(id+"F0.wireOp",EDGE,"E23.filletArc");var subQ11=sQuery(id+"F0.wireOp",EDGE,"E24.filletArc");Q0=makeQuery(id+"F2.boolean.opBoolean","SPLIT",FACE,{"disambiguationData":[TD([makeQuery(id+"F1.opExtrude","SWEPT_FACE",FACE,{"disambiguationData":[OSD([subQ6])]})])],"derivedFrom":makeQuery(id+"F1.opExtrude","CAP_FACE",FACE,{"disambiguationData":[OSD([subQ6,subQ8,subQ9,subQ7,subQ4,subQ3,subQ2,subQ1,subQ0,subQ5,subQ10,subQ11])],"isStart":true})});}
            var sketch = newSketch(context, id + "F16", { "sketchPlane" : qUnion([Q0])});
            skSolve(sketch);
        }
        {
            var Q0;
            Q0=makeQuery(id+"F16.imprint","IMPRINT",FACE,{"disambiguationData":[TD([[makeQuery(id+"F16.imprint","IMPRINT",EDGE,{"derivedFrom":makeQuery(id+"F1.opExtrude","CAP_EDGE",EDGE,{"disambiguationData":[OSD([sQuery(id+"F0.wireOp",EDGE,"E1.bottom")])],"isStart":true})}),1.0]])]});
            var sketch = newSketch(context, id + "F17", { "sketchPlane" : qUnion([Q0])});
            skLineSegment(sketch, "E79.0.0", {"start": v(70, 90) * mm, "end": v(-70, 90) * mm});
            skArc(sketch, "E79.0.1", {"start": v(-70, 90) * mm, "mid": v(-77.07, 87.07) * mm, "end": v(-80, 80) * mm});
            skLineSegment(sketch, "E79.0.2", {"start": v(-80, 80) * mm, "end": v(-80, -80) * mm});
            skArc(sketch, "E79.0.3", {"start": v(-80, -80) * mm, "mid": v(-77.07, -87.07) * mm, "end": v(-70, -90) * mm});
            skLineSegment(sketch, "E79.0.4", {"start": v(-70, -90) * mm, "end": v(70, -90) * mm});
            skArc(sketch, "E79.0.5", {"start": v(70, -90) * mm, "mid": v(77.07, -87.07) * mm, "end": v(80, -80) * mm});
            skLineSegment(sketch, "E79.0.6", {"start": v(80, -80) * mm, "end": v(80, 80) * mm});
            skArc(sketch, "E79.0.7", {"start": v(80, 80) * mm, "mid": v(77.07, 87.07) * mm, "end": v(70, 90) * mm});
            skLineSegment(sketch, "E80", {"start": v(-33, 90) * mm, "end": v(-15, 108) * mm});
            skLineSegment(sketch, "E81", {"start": v(-15, 108) * mm, "end": v(-15, 120) * mm});
            skArc(sketch, "E82", {"start": v(15, 120) * mm, "mid": v(0, 135) * mm, "end": v(-15, 120) * mm});
            skLineSegment(sketch, "E83", {"start": v(15, 120) * mm, "end": v(15, 108) * mm});
            skCircle(sketch, "E84", {"center": v(0, 120) * mm, "radius": 6 * mm});
            skLineSegment(sketch, "E85", {"start": v(0, 90) * mm, "end": v(0, 120) * mm, "construction": true});
            skPoint(sketch, "E85.endSnap0", {"position": v(0, 57.75) * mm});
            skLineSegment(sketch, "E86", {"start": v(15, 108) * mm, "end": v(33, 90) * mm});
            skLineSegment(sketch, "E87", {"start": v(-118.1, 0) * mm, "end": v(117.91, 0) * mm, "construction": true});
            skPoint(sketch, "E87.endSnap0", {"position": v(80, 0) * mm});
            skLineSegment(sketch, "E88.MirrorCS", {"start": v(-80, -80) * mm, "end": v(-80, 80) * mm});
            skArc(sketch, "E89.MirrorCS", {"start": v(15, -120) * mm, "mid": v(0, -135) * mm, "end": v(-15, -120) * mm});
            skLineSegment(sketch, "E90.MirrorCS", {"start": v(-15, -108) * mm, "end": v(-15, -120) * mm});
            skLineSegment(sketch, "E91.MirrorCS", {"start": v(-33, -90) * mm, "end": v(-15, -108) * mm});
            skLineSegment(sketch, "E92.MirrorCS", {"start": v(15, -120) * mm, "end": v(15, -108) * mm});
            skLineSegment(sketch, "E93.MirrorCS", {"start": v(15, -108) * mm, "end": v(33, -90) * mm});
            skLineSegment(sketch, "E94.MirrorCS", {"start": v(0, -90) * mm, "end": v(0, -120) * mm, "construction": true});
            skCircle(sketch, "E95.MirrorC", {"center": v(0, -120) * mm, "radius": 6 * mm});
            skSolve(sketch);
        }
        {
            var Q0;
            Q0=makeQuery(id+"F16.imprint","IMPRINT",FACE,{"disambiguationData":[TD([[makeQuery(id+"F16.imprint","IMPRINT",EDGE,{"derivedFrom":makeQuery(id+"F1.opExtrude","CAP_EDGE",EDGE,{"disambiguationData":[OSD([sQuery(id+"F0.wireOp",EDGE,"E1.bottom")])],"isStart":true})}),1.0]])]});
            var Q1;
            {var subQ0=sQuery(id+"F17.wireOp",EDGE,"E80");Q1=makeQuery(id+"F17.imprint","IMPRINT",FACE,{"disambiguationData":[TD([[makeQuery(id+"F17.imprint","IMPRINT",EDGE,{"derivedFrom":subQ0}),-1.0]])]});}
            var Q2;
            Q2=makeQuery(id+"F17.imprint","IMPRINT",FACE,{"disambiguationData":[TD([[makeQuery(id+"F17.imprint","IMPRINT",EDGE,{"derivedFrom":sQuery(id+"F17.wireOp",EDGE,"E89.MirrorCS")}),-1.0]])]});
            var Q3;
            Q3=makeQuery(id+"F2.opExtrude","CAP_FACE",FACE,{"disambiguationData":[OSD([sQuery(id+"F0.wireOp",EDGE,"E12"),sQuery(id+"F0.wireOp",EDGE,"E13"),sQuery(id+"F0.wireOp",EDGE,"E14"),sQuery(id+"F0.wireOp",EDGE,"E15"),sQuery(id+"F0.wireOp",EDGE,"E17.filletArc"),sQuery(id+"F0.wireOp",EDGE,"E18.filletArc"),sQuery(id+"F0.wireOp",EDGE,"E19.filletArc"),sQuery(id+"F0.wireOp",EDGE,"E20.filletArc"),sQuery(id+"F0.wireOp",EDGE,"E25.0"),sQuery(id+"F0.wireOp",EDGE,"E25.1"),sQuery(id+"F0.wireOp",EDGE,"E25.2"),sQuery(id+"F0.wireOp",EDGE,"E25.3"),sQuery(id+"F0.wireOp",EDGE,"E25.4"),sQuery(id+"F0.wireOp",EDGE,"E25.5"),sQuery(id+"F0.wireOp",EDGE,"E25.6"),sQuery(id+"F0.wireOp",EDGE,"E25.7")])],"isStart":false});
            extrude(context, id + "F18", {"entities" : qUnion([Q0, Q1, Q2]), "endBound" : BoundingType.UP_TO_SURFACE, "endBoundEntityFace" : qUnion([Q3]), "depth" : 25 * mm});
        }
    });
